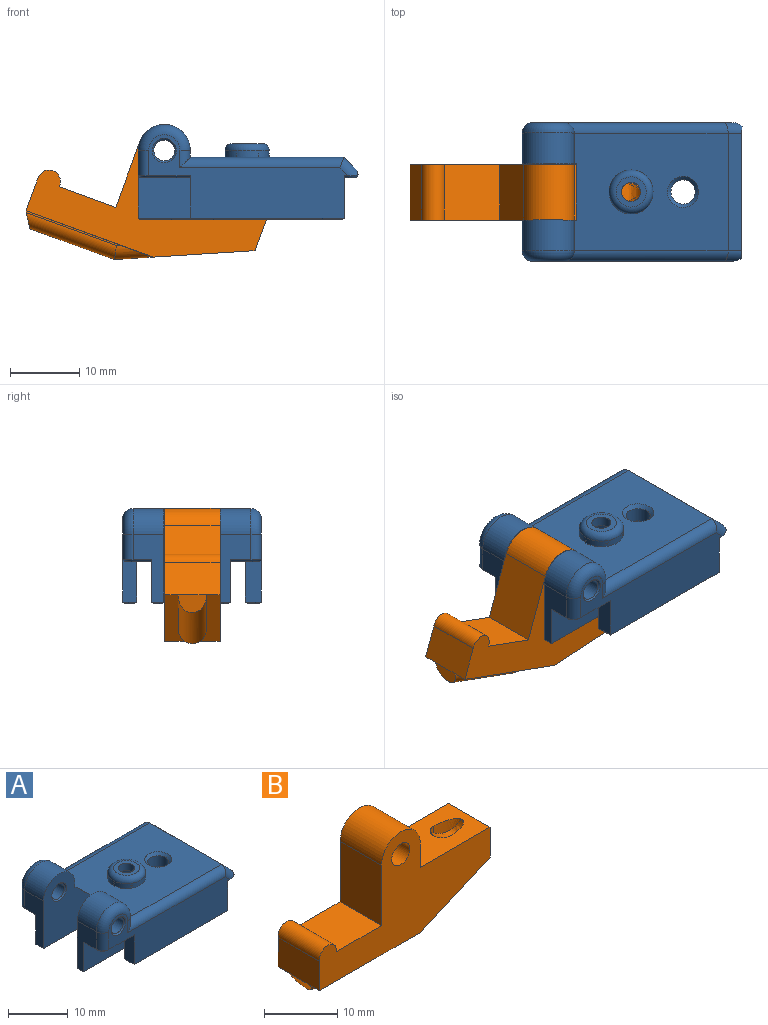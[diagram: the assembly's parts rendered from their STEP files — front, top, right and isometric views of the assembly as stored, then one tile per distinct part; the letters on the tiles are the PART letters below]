
ASSEMBLY  parts=2 mates=1
PART A: 87 faces, bbox 32.4x20.2x14.2 mm
  f0: cylinder r=1.38mm len=2.75mm, axis (0,0,1), area 13mm2, adj f32,f40
  f1: plane 28.73x12mm, normal (0,1,0), area 177.4mm2, adj f23,f29,f48,f49,f50,f51,f52,f59
  f2: plane 22.2x5.85mm, normal (0,-1,0), area 129.9mm2, adj f21,f23,f29,f73
  f3: plane 22.2x5.85mm, normal (0,1,0), area 129.9mm2, adj f21,f26,f28,f84
  f4: plane 29.2x1.25mm, normal (0,0,-1), area 36.5mm2, adj f75,f76,f77,f78
  f5: plane 29.2x0.95mm, normal (0,0,-1), area 27.7mm2, adj f79,f80,f81,f82
  f6: plane 19.14x0.83mm, normal (1,0,0), area 12mm2, adj f41,f47,f52,f61,f62,f64
  f7: plane 28.73x12mm, normal (0,-1,0), area 177.4mm2, adj f26,f28,f43,f44,f45,f46,f47,f56
  f8: plane 29.7x13.5mm, normal (0,1,0), area 220.5mm2, adj f15,f16,f17,f18,f21,f25,f42,f55
  f9: plane 29.7x13.5mm, normal (0,-1,0), area 220.5mm2, adj f10,f11,f12,f15,f21,f22,f42,f55
  f10: plane 4.45x1mm, normal (1,0,0), area 4.5mm2, adj f9,f11,f15,f50
  f11: cylinder r=3.75mm len=7.5mm, axis (0,1,0), area 52.4mm2, adj f9,f10,f12,f49
  f12: plane 9.75x4.45mm, normal (-1,0,0), area 26.9mm2, adj f9,f11,f24,f48,f70,f75
  f13: plane 21.7x1.5mm, normal (0,0,-1), area 32.5mm2, adj f71,f72,f73,f74
  f14: cylinder r=1.5mm len=5.45mm, axis (0,1,0), area 51.4mm2, adj f57,f59
  f15: plane 22.2x17mm, normal (0,0,1), area 327.4mm2, adj f8,f9,f10,f16,f31,f34,f35,f36
  f16: plane 4.45x1mm, normal (1,0,0), area 4.5mm2, adj f8,f15,f17,f45
  f17: cylinder r=3.75mm len=7.5mm, axis (0,1,0), area 52.4mm2, adj f8,f16,f18,f44
  f18: plane 9.75x4.45mm, normal (-1,0,0), area 25.1mm2, adj f8,f17,f27,f43,f67,f79
  f19: plane 21.7x1.8mm, normal (0,0,-1), area 39.1mm2, adj f83,f84,f85,f86
  f20: cylinder r=1.5mm len=5.45mm, axis (0,1,0), area 51.4mm2, adj f56,f58
  f21: plane 31.21x19.51mm, normal (0,0,-1), area 304.6mm2, adj f2,f3,f8,f9,f22,f23,f24,f25
  f22: plane 5.85x1.75mm, normal (1,0,0), area 10.2mm2, adj f9,f21,f24,f78
  f23: plane 6.1x2mm, normal (1,0,0), area 11.7mm2, adj f1,f2,f21,f63,f74
  f24: plane 29.7x6.1mm, normal (0,1,0), area 173.8mm2, adj f12,f21,f22,f70,f76
  f25: plane 5.85x1.45mm, normal (1,0,0), area 8.5mm2, adj f8,f21,f27,f82
  f26: plane 6.1x2.3mm, normal (1,0,0), area 13.5mm2, adj f3,f7,f21,f60,f86
  f27: plane 29.7x6.1mm, normal (0,-1,0), area 173.8mm2, adj f18,f21,f25,f67,f81
  f28: plane 6.1x2.3mm, normal (-1,0,0), area 13.5mm2, adj f3,f7,f21,f65,f83
  f29: plane 6.1x2mm, normal (-1,0,0), area 11.7mm2, adj f1,f2,f21,f68,f71
  f30: cylinder r=1.75mm len=3.5mm, axis (0,0,1), area 23.6mm2, adj f53,f54
  f31: cylinder r=3.17mm len=6.35mm, axis (0,0,-1), area 19.9mm2, adj f15,f33,f34,f35,f36,f37,f38,f39
  f32: plane 4.35x4.35mm, normal (0,0,1), area 8.9mm2, adj f0,f33
  f33: torus R=2.17mm, axis (0,0,1), area 27.7mm2, adj f31,f32
  f34: plane 3.4x2.75mm, normal (-0.87,-0.5,0), area 10.8mm2, adj f15,f21,f31,f35,f39,f40
  f35: plane 3.4x2.75mm, normal (-0.87,0.5,0), area 10.8mm2, adj f15,f21,f31,f34,f36,f40
  f36: plane 3.4x3.18mm, normal (0,1,0), area 10.8mm2, adj f15,f21,f31,f35,f37,f40
  f37: plane 3.4x2.75mm, normal (0.87,0.5,0), area 10.8mm2, adj f15,f21,f31,f36,f38,f40
  f38: plane 3.4x2.75mm, normal (0.87,-0.5,0), area 10.8mm2, adj f15,f21,f31,f37,f39,f40
  f39: plane 3.4x3.18mm, normal (0,-1,0), area 10.8mm2, adj f15,f21,f31,f34,f38,f40
  f40: plane 6.35x5.5mm, normal (0,0,-1), area 20.3mm2, adj f0,f31,f34,f35,f36,f37,f38,f39
  f41: plane 17x2mm, normal (0.71,0,0.71), area 48.1mm2, adj f6,f15,f47,f52
  f42: plane 8.1x2.83mm, normal (-0.71,0,-0.71), area 32.4mm2, adj f8,f9,f15,f55
  f43: cylinder r=1.5mm len=3.65mm, axis (0,0,1), area 8.6mm2, adj f7,f18,f44,f66
  f44: torus R=2.25mm, axis (0,-1,0), area 23.7mm2, adj f7,f17,f43,f45
  f45: cylinder r=1.5mm len=2.5mm, axis (0,0,-1), area 4.1mm2, adj f7,f16,f44,f46
  f46: cylinder r=1.5mm len=23.7mm, axis (1,0,0), area 53.3mm2, adj f7,f15,f45,f47
  f47: cylinder r=1.5mm len=3.32mm, axis (-0.71,0,0.71), area 6mm2, adj f6,f7,f41,f46,f61
  f48: cylinder r=1.5mm len=3.65mm, axis (0,0,-1), area 8.6mm2, adj f1,f12,f49,f69
  f49: torus R=2.25mm, axis (0,-1,0), area 23.7mm2, adj f1,f11,f48,f50
  f50: cylinder r=1.5mm len=2.5mm, axis (0,0,1), area 4.1mm2, adj f1,f10,f49,f51
  f51: cylinder r=1.5mm len=23.7mm, axis (-1,0,0), area 53.3mm2, adj f1,f15,f50,f52
  f52: cylinder r=1.5mm len=3.32mm, axis (-0.71,0,0.71), area 6mm2, adj f1,f6,f41,f51,f64
  f53: cone r=1.75mm half-angle=45deg, axis (0,0,1), area 8.9mm2, adj f15,f30
  f54: cone r=2mm half-angle=45deg, axis (0,0,-1), area 4.2mm2, adj f21,f30
  f55: plane 8.1x0.18mm, normal (-0.38,0,-0.92), area 1.5mm2, adj f8,f9,f21,f42
  f56: cone r=1.5mm half-angle=45deg, axis (0,-1,0), area 3.6mm2, adj f7,f20
  f57: cone r=1.5mm half-angle=45deg, axis (0,-1,0), area 3.6mm2, adj f9,f14
  f58: cone r=1.75mm half-angle=45deg, axis (0,1,0), area 3.6mm2, adj f8,f20
  f59: cone r=1.75mm half-angle=45deg, axis (0,1,0), area 3.6mm2, adj f1,f14
  f60: plane 0.53x0.25mm, normal (0,-0.71,-0.71), area 0.2mm2, adj f7,f21,f26,f61
  f61: bspline ~1.67x0.86mm, area 0.6mm2, adj f6,f21,f47,f60,f62
  f62: plane 18.94x0.38mm, normal (0.71,0,-0.71), area 6.6mm2, adj f6,f21,f61,f64
  f63: plane 0.53x0.25mm, normal (0,0.71,-0.71), area 0.2mm2, adj f1,f21,f23,f64
  f64: bspline ~1.67x0.86mm, area 0.6mm2, adj f6,f21,f52,f62,f63
  f65: plane 6x0.25mm, normal (0,-0.71,-0.71), area 2.1mm2, adj f7,f21,f28,f66
  f66: cone r=1.25mm half-angle=45deg, axis (0,0,1), area 0.8mm2, adj f21,f43,f65,f67
  f67: plane 3x0.25mm, normal (-0.71,0,-0.71), area 1.1mm2, adj f18,f21,f27,f66
  f68: plane 6x0.25mm, normal (0,0.71,-0.71), area 2.1mm2, adj f1,f21,f29,f69
  f69: cone r=1.25mm half-angle=45deg, axis (0,0,1), area 0.8mm2, adj f21,f48,f68,f70
  f70: plane 2.7x0.25mm, normal (-0.71,0,-0.71), area 1mm2, adj f12,f21,f24,f69
  f71: plane 2x0.25mm, normal (-0.71,0,-0.71), area 0.6mm2, adj f13,f29,f72,f73
  f72: plane 22.2x0.25mm, normal (0,0.71,-0.71), area 7.8mm2, adj f1,f13,f71,f74
  f73: plane 22.2x0.25mm, normal (0,-0.71,-0.71), area 7.8mm2, adj f2,f13,f71,f74
  f74: plane 2x0.25mm, normal (0.71,0,-0.71), area 0.6mm2, adj f13,f23,f72,f73
  f75: plane 1.75x0.25mm, normal (-0.71,0,-0.71), area 0.5mm2, adj f4,f12,f76,f77
  f76: plane 29.7x0.25mm, normal (0,0.71,-0.71), area 10.4mm2, adj f4,f24,f75,f78
  f77: plane 29.7x0.25mm, normal (0,-0.71,-0.71), area 10.4mm2, adj f4,f9,f75,f78
  f78: plane 1.75x0.25mm, normal (0.71,0,-0.71), area 0.5mm2, adj f4,f22,f76,f77
  f79: plane 1.45x0.25mm, normal (-0.71,0,-0.71), area 0.4mm2, adj f5,f18,f80,f81
  f80: plane 29.7x0.25mm, normal (0,0.71,-0.71), area 10.4mm2, adj f5,f8,f79,f82
  f81: plane 29.7x0.25mm, normal (0,-0.71,-0.71), area 10.4mm2, adj f5,f27,f79,f82
  f82: plane 1.45x0.25mm, normal (0.71,0,-0.71), area 0.4mm2, adj f5,f25,f80,f81
  f83: plane 2.3x0.25mm, normal (-0.71,0,-0.71), area 0.7mm2, adj f19,f28,f84,f85
  f84: plane 22.2x0.25mm, normal (0,0.71,-0.71), area 7.8mm2, adj f3,f19,f83,f86
  f85: plane 22.2x0.25mm, normal (0,-0.71,-0.71), area 7.8mm2, adj f7,f19,f83,f86
  f86: plane 2.3x0.25mm, normal (0.71,0,-0.71), area 0.7mm2, adj f19,f26,f84,f85
PART B: 24 faces, bbox 33x8x21 mm
  f0: plane 19.5x4mm, normal (0,0,-1), area 41.1mm2, adj f7,f9,f13,f16,f17
  f1: plane 13.5x8mm, normal (0,0,1), area 93.9mm2, adj f2,f10,f12,f13,f19,f20,f21,f22
  f2: plane 8x4.1mm, normal (1,0,0), area 32.8mm2, adj f1,f3,f12,f13
  f3: cylinder r=3.75mm len=8mm, axis (0,1,0), area 94.2mm2, adj f2,f4,f12,f13
  f4: plane 10.1x8mm, normal (-1,0,0), area 80.8mm2, adj f3,f5,f12,f13
  f5: plane 8.69x8mm, normal (0,0,1), area 69.6mm2, adj f4,f6,f12,f13
  f6: cylinder r=1.66mm len=8mm, axis (0,1,0), area 45mm2, adj f5,f7,f12,f13
  f7: plane 8x4.9mm, normal (-1,0,0), area 39.2mm2, adj f0,f6,f8,f12,f13,f14
  f8: plane 19.5x4mm, normal (0,0,-1), area 41.1mm2, adj f7,f9,f12,f15,f17
  f9: plane 13.5x8mm, normal (0.4,0,-0.92), area 117.9mm2, adj f0,f8,f10,f12,f13
  f10: plane 8x5mm, normal (1,0,0), area 40mm2, adj f1,f9,f12,f13
  f11: cylinder r=1.75mm len=8mm, axis (0,1,0), area 88mm2, adj f12,f13
  f12: plane 33.01x18.75mm, normal (0,-1,0), area 296.1mm2, adj f1,f2,f3,f4,f5,f6,f7,f8
  f13: plane 33.01x18.75mm, normal (0,1,0), area 296.1mm2, adj f0,f1,f2,f3,f4,f5,f6,f7
  f14: plane 4x2.23mm, normal (-0.85,0,-0.53), area 8.5mm2, adj f7,f15,f16,f18
  f15: plane 14.51x0.23mm, normal (0,-1,0), area 3.3mm2, adj f8,f14,f17,f18
  f16: plane 14.51x0.23mm, normal (0,1,0), area 3.3mm2, adj f0,f14,f17,f18
  f17: cylinder r=2mm len=5.92mm, axis (0.92,0,0.4), area 23.7mm2, adj f0,f8,f15,f16,f18
  f18: cylinder r=2mm len=14.24mm, axis (-1,0,0), area 83.6mm2, adj f14,f15,f16,f17
  f19: extruded ~3.87x1.95mm, area 6.6mm2, adj f1,f22,f23
  f20: extruded ~3.87x1.95mm, area 6.6mm2, adj f1,f21,f23
  f21: cylinder r=1.65mm len=1.64mm, axis (0,0,1), area 1.1mm2, adj f1,f20,f23
  f22: cylinder r=1.65mm len=1.64mm, axis (0,0,1), area 1.1mm2, adj f1,f19,f23
  f23: extruded ~5.46x3.29mm, area 16.8mm2, adj f19,f20,f21,f22
PLACE A at identity fixed
PLACE B rot(axis=(0,1,0),20deg) t=(-2.74,-0.05,0.48)mm
MATE revolute A.f11 <-> B.f3  axis (0,1,0) through (0,-4.05,8)mm
